# Revit family: Faucet-Kitchen_Sink-KOHLER-Barossa-K-R78035
name_source: partatom
category: Plumbing Fixtures
revit_build: Autodesk Revit 2015 (Build: 20140606_1530(x64)
units: mm (PartAtom-declared; Revit-internal decimal feet)

## types (1)
- VS- Vibrant Stainless
    ADA Compliant = Yes
    Apparent Load = 0 VA
    Assembly Code = D2010
    CW Connection = Yes
    Cold Water Inlet = Cold Water Inlet
    Date Modified = 03/29/2018
    Default Elevation = 36"
    Description = Touchless pull-down kitchen faucet with soap/lotion dispenser
    Electrical Connector = Yes
    Electrical Note = 120V AC Required if batteries are not used
    Finish = Kohler-Metal-VS-Vibrant_Stainless
    Flow Rate = 2 GPM
    HW Connection = Yes
    Height = 15 1/4"
    Hot Water Inlet = Hot Water Inlet
    Length = 11 1/8"
    Manufacturer = KOHLER Co.
    MasterFormat 1995 = 15410
    MasterFormat 2004 = 22.41.39
    Material = Premium metal construction
    Model = K-R78035-SD-VS
    Pressure = 60.00 psi
    Product Documentation Link = http://www.us.kohler.com
    Product Name = Barossa
    Product Page URL = http://www.us.kohler.com
    Spout Reach = 9 1/32"
    URL = https://www.us.kohler.com
    Vent Connection = No
    Voltage = 120 V
    Waste Connection = No
    Waste Water Outlet = Waste Water Outlet

## geometry (parser evidence)
native form markers: Sweep x9
no freeform markers — native parametric forms only
